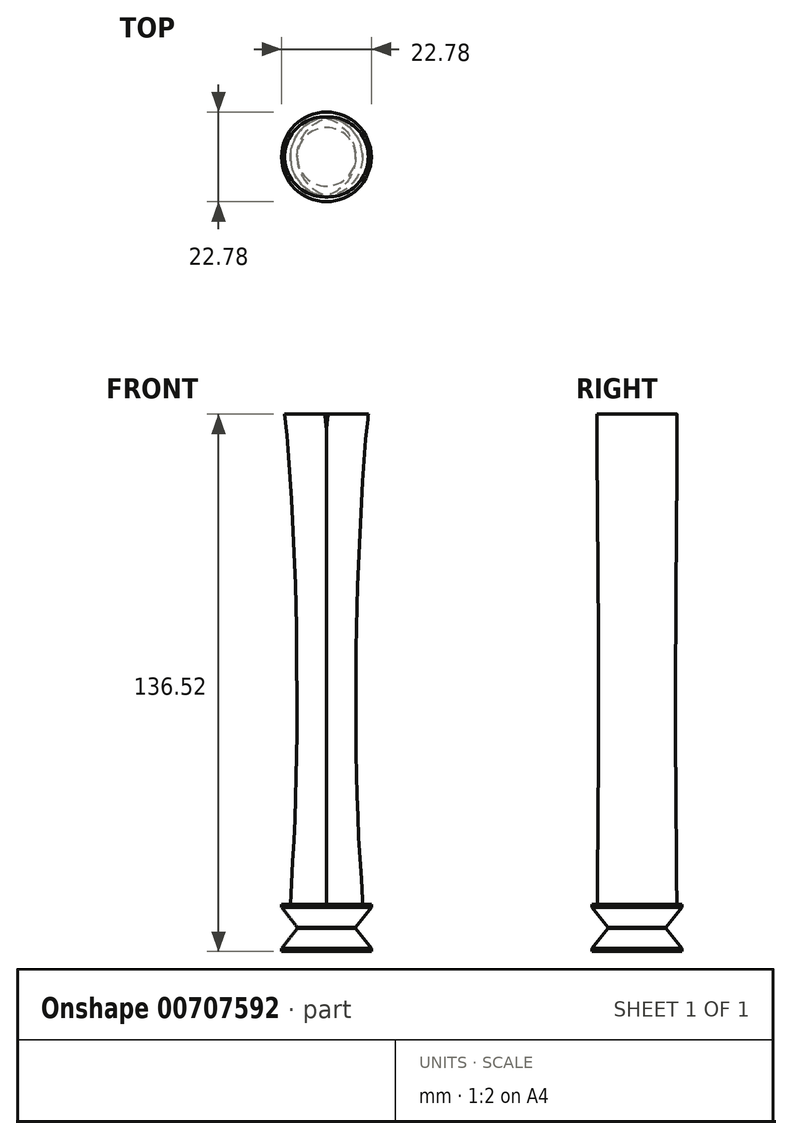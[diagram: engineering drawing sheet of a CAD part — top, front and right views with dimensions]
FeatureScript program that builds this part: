
annotation { "Feature Type Name" : "Feature", "Feature Type Description" : "" }
export const myFeature = defineFeature(function(context is Context, id is Id, definition is map)
    precondition{}
    {
        {
            var Q0;
            Q0=qCreatedBy(makeId("Front.planeOp"),FACE);
            var sketch = newSketch(context, id + "F0", { "sketchPlane" : qUnion([Q0])});
            skLineSegment(sketch, "E0", {"start": v(11.7, 8.56) * mm, "end": v(10.7, -7.18) * mm});
            skLineSegment(sketch, "E1", {"start": v(10.7, -7.18) * mm, "end": v(-10.6, 19) * mm});
            skLineSegment(sketch, "E2", {"start": v(-10.6, 19) * mm, "end": v(-7.8, 82.36) * mm});
            skFitSpline(sketch, "E3", {"points": [v(-7.8, 82.36) * mm, v(-7.24, 98.94) * mm, v(-6.59, 117.12) * mm, v(-5.83, 142.02) * mm, v(-5.45, 168.32) * mm, v(-5.52, 230.34) * mm, v(-6.26, 285.7) * mm, v(-7.2, 315.28) * mm, v(-8.95, 361.43) * mm, v(-10.4, 387.63) * mm, v(-13, 416.84) * mm, v(-15.01, 437.7) * mm, v(-21.29, 480.96) * mm, v(-27.2, 508.68) * mm, v(-28.7, 514.88) * mm], "startDerivative": vector(10.22, 308.11) * mm, "endDerivative": vector(-37.95, 155.7) * mm});
            skLineSegment(sketch, "E4", {"start": v(-28.7, 514.88) * mm, "end": v(-18.5, 504.49) * mm});
            skFitSpline(sketch, "E5", {"points": [v(-18.5, 504.49) * mm, v(-14.2, 494.72) * mm, v(-10.4, 483.17) * mm, v(-6.54, 469.9) * mm, v(-3.1, 457.05) * mm, v(-0.51, 445.6) * mm, v(1.47, 435.93) * mm, v(2.96, 426.2) * mm, v(4.35, 415.6) * mm, v(5.85, 403.15) * mm, v(7.18, 390.92) * mm, v(9.67, 369.53) * mm, v(11.56, 352.56) * mm, v(15.2, 318.42) * mm, v(18.03, 290.8) * mm, v(19.92, 265.34) * mm, v(21.72, 242.6) * mm, v(22.69, 220.79) * mm, v(23.65, 203.25) * mm, v(24.47, 178.85) * mm, v(25.08, 148.77) * mm, v(25.19, 106.94) * mm, v(24.82, 74.57) * mm, v(24.5, 42) * mm], "startDerivative": vector(138.63, -295.52) * mm, "endDerivative": vector(-5.12, -584.15) * mm});
            skFitSpline(sketch, "E6", {"points": [v(24.5, 42) * mm, v(16.7, 39) * mm, v(12.5, 33.24) * mm, v(9.61, 24.95) * mm, v(8.9, 16.91) * mm, v(10.33, 12.23) * mm, v(11.7, 8.56) * mm], "startDerivative": vector(-46.28, -12) * mm, "endDerivative": vector(10.21, -28.51) * mm});
            skFitSpline(sketch, "E7", {"points": [v(-10.6, 84.98) * mm, v(-8.5, 83) * mm, v(-6.65, 78.8) * mm, v(-5.89, 72.07) * mm, v(-5.76, 61.33) * mm, v(-5.64, 47.1) * mm, v(-5.9, 35.6) * mm, v(-6.47, 31.43) * mm, v(-6.34, 26.97) * mm, v(-4.57, 21.8) * mm, v(-2.21, 17.83) * mm, v(0, 15.05) * mm, v(2.28, 13.08) * mm, v(5.76, 11.32) * mm, v(8.69, 10.16) * mm, v(11.04, 8.9) * mm, v(12.38, 7.6) * mm, v(13.09, 5.99) * mm, v(12.89, 2.76) * mm, v(12.15, -3.9) * mm, v(11.7, -8.74) * mm, v(11.08, -13.22) * mm], "startDerivative": vector(59.9, -45.86) * mm, "endDerivative": vector(-14.62, -97.53) * mm});
            skLineSegment(sketch, "E8", {"start": v(11.08, -13.22) * mm, "end": v(11.08, -15.97) * mm});
            skLineSegment(sketch, "E9", {"start": v(11.08, -15.97) * mm, "end": v(-11.03, -15.97) * mm});
            skLineSegment(sketch, "E10", {"start": v(-11.03, -15.97) * mm, "end": v(-11.2, -13.29) * mm});
            skFitSpline(sketch, "E11", {"points": [v(-11.2, -13.29) * mm, v(-11.2, -11.84) * mm, v(-11.2, -5.52) * mm, v(-11.51, 1.49) * mm, v(-12.16, 4.66) * mm, v(-13.4, 9.05) * mm, v(-15.15, 13.55) * mm, v(-16.64, 17.33) * mm, v(-19.12, 23.61) * mm, v(-19.55, 26.56) * mm, v(-18.64, 31.28) * mm, v(-16.79, 35.33) * mm, v(-14.77, 40.57) * mm, v(-13.5, 46.17) * mm, v(-12.6, 53.4) * mm, v(-12.2, 59.96) * mm, v(-12.37, 65.97) * mm, v(-12.16, 73.91) * mm, v(-11.5, 81.04) * mm, v(-11.2, 84.64) * mm, v(-10.6, 84.98) * mm], "startDerivative": vector(-0.12, 43.3) * mm, "endDerivative": vector(35.61, 8.6) * mm});
            skFitSpline(sketch, "E12", {"points": [v(11.08, -13.22) * mm, v(15.57, -17.52) * mm, v(22.06, -24.41) * mm, v(29.6, -33.47) * mm, v(35.84, -41.56) * mm, v(40.17, -47.64) * mm, v(44.57, -55.74) * mm, v(47.94, -62.06) * mm, v(51.06, -67.51) * mm, v(52.42, -69.67) * mm, v(49.81, -81.38) * mm, v(45.5, -94.07) * mm, v(41.24, -106.63) * mm, v(36.2, -120.43) * mm, v(32.84, -130.03) * mm, v(29.35, -138.2) * mm, v(27.78, -142.23) * mm, v(23.27, -152.08) * mm, v(21.3, -154.75) * mm, v(16.02, -157.43) * mm, v(8.58, -160.03) * mm, v(4.77, -160.41) * mm, v(4.83, -154.75) * mm, v(8.26, -152.78) * mm, v(13.03, -150.3) * mm, v(16.97, -147.44) * mm, v(20.66, -141.85) * mm, v(25.37, -129.07) * mm, v(31.66, -108.36) * mm, v(36.51, -89.69) * mm, v(39.56, -77.02) * mm, v(39.75, -72.83) * mm, v(38.74, -67.42) * mm, v(35.21, -61.22) * mm, v(28.26, -50.55) * mm, v(23.02, -43.89) * mm, v(18.43, -38.21) * mm, v(13.22, -32.69) * mm, v(7.93, -27.32) * mm, v(6.6, -20.94) * mm, v(11.08, -13.22) * mm]});
            skLineSegment(sketch, "E13.bottom", {"start": v(-12.44, -13.29) * mm, "end": v(11.54, -13.29) * mm});
            skLineSegment(sketch, "E13.top", {"start": v(-12.44, -29.01) * mm, "end": v(11.54, -29.01) * mm});
            skLineSegment(sketch, "E13.left", {"start": v(-12.44, -13.29) * mm, "end": v(-12.44, -29.01) * mm});
            skLineSegment(sketch, "E13.right", {"start": v(11.54, -13.29) * mm, "end": v(11.54, -29.01) * mm});
            skLineSegment(sketch, "E14", {"start": v(0, -32.56) * mm, "end": v(0, -38.28) * mm});
            skFitSpline(sketch, "E15", {"points": [v(-10.75, -28.03) * mm, v(-9.93, -35.6) * mm, v(-9.25, -45.2) * mm, v(-8.25, -64.06) * mm, v(-7.6, -83.45) * mm, v(-7.55, -95.02) * mm, v(-7.45, -109.5) * mm, v(-7.73, -122.65) * mm, v(-8.29, -138.57) * mm, v(-9.14, -152.56) * mm, v(-9.03, -155.04) * mm], "startDerivative": vector(11.05, -94.6) * mm, "endDerivative": vector(4.37, -43.01) * mm});
            skLineSegment(sketch, "E16", {"start": v(-9.9, -153.6) * mm, "end": v(9.57, -153.6) * mm});
            skFitSpline(sketch, "E17.MirrorCS", {"points": [v(10.75, -28.03) * mm, v(9.93, -35.6) * mm, v(9.25, -45.2) * mm, v(8.25, -64.06) * mm, v(7.6, -83.45) * mm, v(7.55, -95.02) * mm, v(7.45, -109.5) * mm, v(7.73, -122.65) * mm, v(8.29, -138.57) * mm, v(9.14, -152.56) * mm, v(9.03, -155.04) * mm], "startDerivative": vector(-11.05, -94.6) * mm, "endDerivative": vector(-4.37, -43.01) * mm});
            skSolve(sketch);
        }
        {
            var Q0;
            {var subQ0=sQuery(id+"F0.wireOp",EDGE,"E16");var subQ5=sQuery(id+"F0.wireOp",EDGE,"E12");var subQ7=makeQuery(id+"F0.imprint","INTERSECT",VERTEX,{"derivedFrom":[subQ5,subQ0]});Q0=makeQuery(id+"F0.imprint","IMPRINT",FACE,{"disambiguationData":[TD([[makeQuery(id+"F0.imprint","IMPRINT",EDGE,{"disambiguationData":[TD([[subQ7,-1.0]])],"derivedFrom":subQ5}),1.0]])]});}
            var Q1;
            {var subQ0=sQuery(id+"F0.wireOp",EDGE,"E17.MirrorCS");var subQ1=sQuery(id+"F0.wireOp",EDGE,"E12");var subQ2=makeQuery(id+"F0.imprint","INTERSECT",VERTEX,{"disambiguationData":[OD(1.0)],"derivedFrom":[subQ1,subQ0]});Q1=makeQuery(id+"F0.imprint","IMPRINT",FACE,{"disambiguationData":[TD([[makeQuery(id+"F0.imprint","IMPRINT",EDGE,{"disambiguationData":[TD([[subQ2,-1.0]])],"derivedFrom":subQ1}),-1.0]])]});}
            var Q2;
            {var subQ0=sQuery(id+"F0.wireOp",EDGE,"E16");var subQ1=sQuery(id+"F0.wireOp",EDGE,"E12");var subQ2=makeQuery(id+"F0.imprint","INTERSECT",VERTEX,{"derivedFrom":[subQ1,subQ0]});Q2=makeQuery(id+"F0.imprint","IMPRINT",FACE,{"disambiguationData":[TD([[makeQuery(id+"F0.imprint","IMPRINT",EDGE,{"disambiguationData":[TD([[subQ2,-1.0]])],"derivedFrom":subQ1}),-1.0]])]});}
            extrude(context, id + "F1", {"entities" : qUnion([Q0, Q1, Q2]), "endBound" : BoundingType.SYMMETRIC, "depth" : 20.32 * mm, "offsetDistance" : 25.4 * mm});
        }
        {
            var Q0;
            Q0=makeQuery(id+"F1.opExtrude","CAP_EDGE",EDGE,{"disambiguationData":[OSD([sQuery(id+"F0.wireOp",EDGE,"E17.MirrorCS")])],"isStart":false});
            var Q1;
            Q1=makeQuery(id+"F1.opExtrude","CAP_EDGE",EDGE,{"disambiguationData":[OSD([sQuery(id+"F0.wireOp",EDGE,"E17.MirrorCS")])],"isStart":true});
            var Q2;
            Q2=makeQuery(id+"F1.opExtrude","CAP_EDGE",EDGE,{"disambiguationData":[OSD([sQuery(id+"F0.wireOp",EDGE,"E15")])],"isStart":true});
            var Q3;
            Q3=makeQuery(id+"F1.opExtrude","CAP_EDGE",EDGE,{"disambiguationData":[OSD([sQuery(id+"F0.wireOp",EDGE,"E15")])],"isStart":false});
            fillet(context, id + "F2", {"entities" : qUnion([Q0, Q1, Q2, Q3]), "radius" : 10.16 * mm, "tangentPropagation" : true, "allowEdgeOverflow" : false});
        }
        {
            var Q0;
            Q0=makeQuery(id+"F1.opExtrude","SWEPT_FACE",FACE,{"disambiguationData":[OSD([sQuery(id+"F0.wireOp",EDGE,"E16")])]});
            var sketch = newSketch(context, id + "F3", { "sketchPlane" : qUnion([Q0])});
            skCircle(sketch, "E18", {"center": v(0, 0) * mm, "radius": 11.4 * mm});
            skSolve(sketch);
        }
        {
            var Q0;
            {var subQ0=makeQuery(id+"F1.opExtrude","SWEPT_FACE",FACE,{"disambiguationData":[OSD([sQuery(id+"F0.wireOp",EDGE,"E16")])]});var subQ1=sQuery(id+"F0.wireOp",EDGE,"E15");Q0=makeQuery(id+"F3.imprint","IMPRINT",FACE,{"disambiguationData":[TD([[makeQuery(id+"F3.imprint","IMPRINT",EDGE,{"derivedFrom":makeQuery(id+"F2.opFillet","BLEND_EDGE",EDGE,{"blendedFrom":[makeQuery(id+"F1.opExtrude","CAP_EDGE",EDGE,{"disambiguationData":[OSD([subQ1])],"isStart":true}),subQ0],"blendedInto":[subQ0]})}),1.0]])]});}
            var Q1;
            Q1=makeQuery(id+"F3.imprint","IMPRINT",FACE,{"disambiguationData":[TD([[makeQuery(id+"F3.imprint","IMPRINT",EDGE,{"derivedFrom":sQuery(id+"F3.wireOp",EDGE,"E18")}),1.0]])]});
            extrude(context, id + "F4", {"entities" : qUnion([Q0, Q1]), "operationType" : NewBodyOperationType.ADD, "depth" : 11.94 * mm, "offsetDistance" : 25.4 * mm});
        }
        {
            var Q0;
            Q0=qCreatedBy(makeId("Front.planeOp"),FACE);
            var sketch = newSketch(context, id + "F5", { "sketchPlane" : qUnion([Q0])});
            skLineSegment(sketch, "E19.bottom", {"start": v(-11.77, -159.36) * mm, "end": v(12.26, -159.36) * mm});
            skLineSegment(sketch, "E19.top", {"start": v(-11.77, -159.68) * mm, "end": v(12.26, -159.68) * mm});
            skLineSegment(sketch, "E19.left", {"start": v(-11.77, -159.36) * mm, "end": v(-11.77, -159.68) * mm});
            skLineSegment(sketch, "E19.right", {"start": v(12.26, -159.36) * mm, "end": v(12.26, -159.68) * mm});
            skSolve(sketch);
        }
        {
            var Q0;
            Q0 = qSketchRegion(id + "F5", true);
            extrude(context, id + "F6", {"entities" : qUnion([Q0]), "operationType" : NewBodyOperationType.REMOVE, "oppositeDirection" : true, "depth" : 25.4 * mm, "offsetDistance" : 25.4 * mm});
        }
        {
            var Q0;
            Q0=makeQuery(id+"F6.boolean.opBoolean","COPY",FACE,{"derivedFrom":makeQuery(id+"F6.opExtrude","CAP_FACE",FACE,{"disambiguationData":[OSD([sQuery(id+"F5.wireOp",EDGE,"E19.bottom"),sQuery(id+"F5.wireOp",EDGE,"E19.top"),sQuery(id+"F5.wireOp",EDGE,"E19.left"),sQuery(id+"F5.wireOp",EDGE,"E19.right")])],"isStart":true})});
            extrude(context, id + "F7", {"entities" : qUnion([Q0]), "operationType" : NewBodyOperationType.REMOVE, "oppositeDirection" : true, "depth" : 25.4 * mm, "offsetDistance" : 25.4 * mm});
        }
        {
            var Q0;
            {var subQ0=sQuery(id+"F5.wireOp",EDGE,"E19.top");Q0=makeQuery(id+"F7.boolean.opBoolean","MERGE",FACE,{"derivedFrom":[makeQuery(id+"F6.boolean.opBoolean","COPY",FACE,{"derivedFrom":makeQuery(id+"F6.opExtrude","SWEPT_FACE",FACE,{"disambiguationData":[OSD([subQ0])]})})],"fromTools":[makeQuery(id+"F7.opExtrude","SWEPT_FACE",FACE,{"disambiguationData":[OSD([subQ0])]})]});}
            var Q1;
            {var subQ0=sQuery(id+"F5.wireOp",EDGE,"E19.bottom");Q1=makeQuery(id+"F7.boolean.opBoolean","MERGE",FACE,{"derivedFrom":[makeQuery(id+"F6.boolean.opBoolean","COPY",FACE,{"derivedFrom":makeQuery(id+"F6.opExtrude","SWEPT_FACE",FACE,{"disambiguationData":[OSD([subQ0])]})})],"fromTools":[makeQuery(id+"F7.opExtrude","SWEPT_FACE",FACE,{"disambiguationData":[OSD([subQ0])]})]});}
            chamfer(context, id + "F8", {"entities" : qUnion([Q0, Q1]), "chamferType" : ChamferType.OFFSET_ANGLE, "width" : 5.08 * mm, "oppositeDirection" : false, "angle" : 38 * degree, "tangentPropagation" : true});
        }
        {
            var Q0;
            {var subQ0=sQuery(id+"F5.wireOp",EDGE,"E19.bottom");Q0=makeQuery(id+"F7.boolean.opBoolean","MERGE",FACE,{"derivedFrom":[makeQuery(id+"F6.boolean.opBoolean","COPY",FACE,{"derivedFrom":makeQuery(id+"F6.opExtrude","SWEPT_FACE",FACE,{"disambiguationData":[OSD([subQ0])]})})],"fromTools":[makeQuery(id+"F7.opExtrude","SWEPT_FACE",FACE,{"disambiguationData":[OSD([subQ0])]})]});}
            extrude(context, id + "F9", {"entities" : qUnion([Q0]), "operationType" : NewBodyOperationType.ADD, "depth" : 2.54 * mm, "offsetDistance" : 25.4 * mm});
        }
    });
